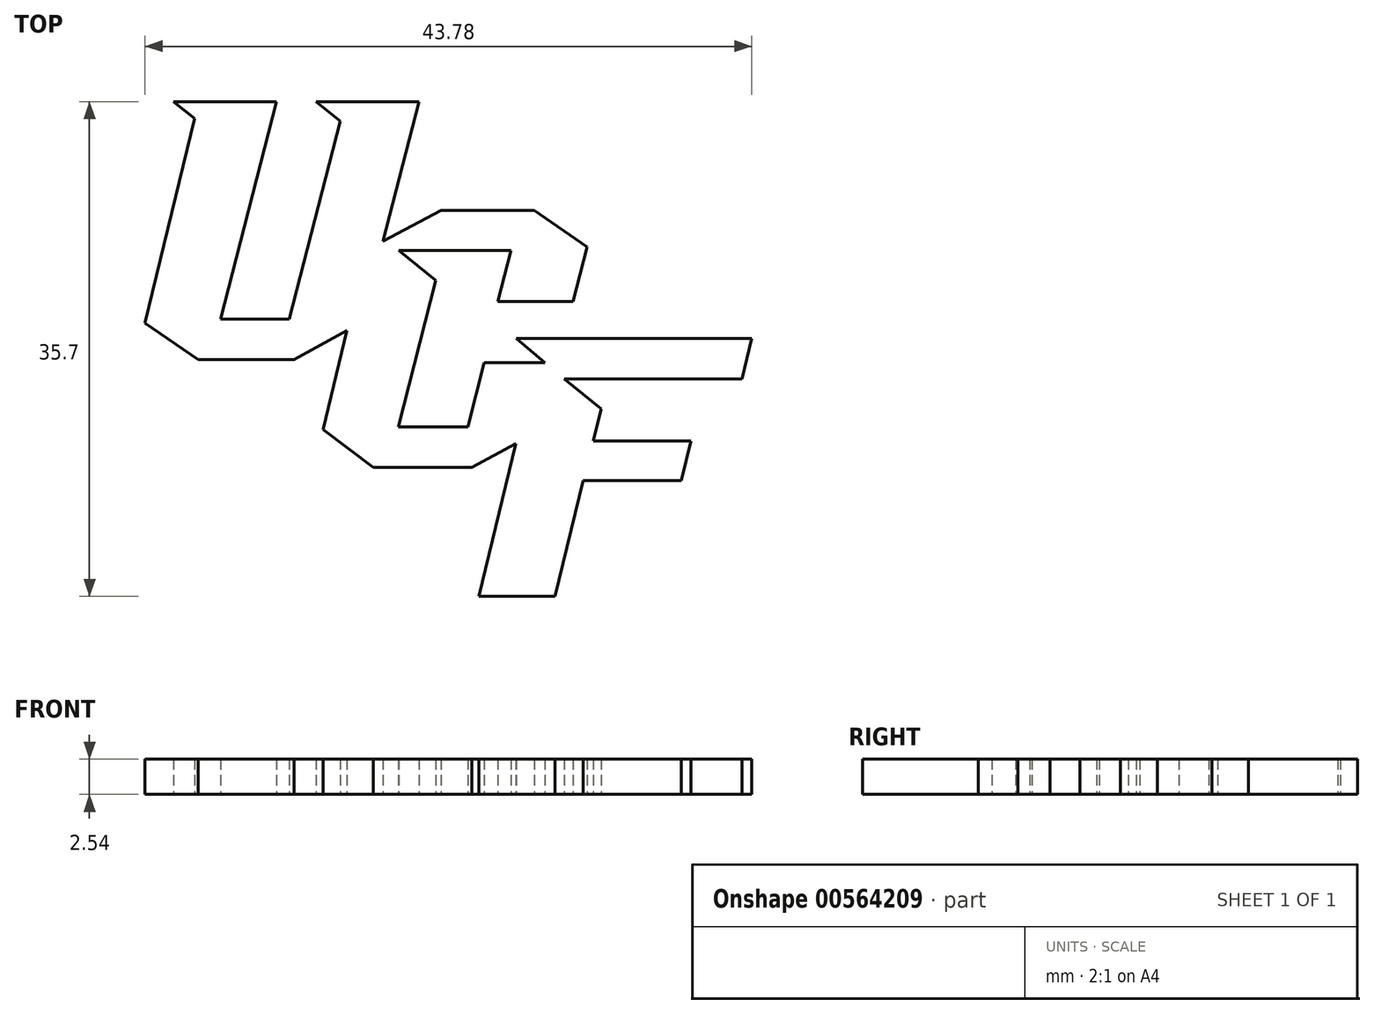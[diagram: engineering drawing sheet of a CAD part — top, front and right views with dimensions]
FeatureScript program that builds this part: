
annotation { "Feature Type Name" : "Feature", "Feature Type Description" : "" }
export const myFeature = defineFeature(function(context is Context, id is Id, definition is map)
    precondition{}
    {
        {
            var Q0;
            Q0=qCreatedBy(makeId("Top.planeOp"),FACE);
            var sketch = newSketch(context, id + "F0", { "sketchPlane" : qUnion([Q0])});
            skLineSegment(sketch, "E0", {"start": v(-24.4, 19.25) * mm, "end": v(2.19, 19.25) * mm});
            skLineSegment(sketch, "E1", {"start": v(2.19, 19.25) * mm, "end": v(0.35, 11.38) * mm});
            skLineSegment(sketch, "E2", {"start": v(0.35, 11.38) * mm, "end": v(8.5, 11.38) * mm});
            skLineSegment(sketch, "E3", {"start": v(8.5, 11.38) * mm, "end": v(14.26, 7.42) * mm});
            skLineSegment(sketch, "E4", {"start": v(14.26, 7.42) * mm, "end": v(12.9, 2.1) * mm});
            skLineSegment(sketch, "E5", {"start": v(12.9, 2.1) * mm, "end": v(26.4, 2.1) * mm});
            skLineSegment(sketch, "E6", {"start": v(26.4, 2.1) * mm, "end": v(24.63, -5.27) * mm});
            skLineSegment(sketch, "E7", {"start": v(24.63, -5.27) * mm, "end": v(21.92, -5.27) * mm});
            skLineSegment(sketch, "E8", {"start": v(21.92, -5.27) * mm, "end": v(20, -12.77) * mm});
            skLineSegment(sketch, "E9", {"start": v(20, -12.77) * mm, "end": v(13.09, -12.77) * mm});
            skLineSegment(sketch, "E10", {"start": v(13.09, -12.77) * mm, "end": v(10.99, -20.97) * mm});
            skLineSegment(sketch, "E11", {"start": v(10.99, -20.97) * mm, "end": v(0.94, -20.97) * mm});
            skLineSegment(sketch, "E12", {"start": v(0.94, -20.97) * mm, "end": v(3.33, -11.66) * mm});
            skLineSegment(sketch, "E13", {"start": v(3.33, -11.66) * mm, "end": v(-4.63, -11.66) * mm});
            skLineSegment(sketch, "E14", {"start": v(-4.63, -11.66) * mm, "end": v(-9.96, -7.66) * mm});
            skLineSegment(sketch, "E15", {"start": v(-9.96, -7.66) * mm, "end": v(-8.96, -3.76) * mm});
            skLineSegment(sketch, "E16", {"start": v(-8.96, -3.76) * mm, "end": v(-17.19, -3.76) * mm});
            skLineSegment(sketch, "E17", {"start": v(-17.19, -3.76) * mm, "end": v(-22.66, 0.35) * mm});
            skLineSegment(sketch, "E18", {"start": v(-22.66, 0.35) * mm, "end": v(-18.94, 14.88) * mm});
            skLineSegment(sketch, "E19", {"start": v(-18.94, 14.88) * mm, "end": v(-24.4, 19.25) * mm});
            skLineSegment(sketch, "E20", {"start": v(-17.04, 15.64) * mm, "end": v(-19.12, 17.3) * mm});
            skLineSegment(sketch, "E21", {"start": v(-19.12, 17.3) * mm, "end": v(-10.38, 17.3) * mm});
            skLineSegment(sketch, "E22", {"start": v(-10.38, 17.3) * mm, "end": v(-14.4, 1.61) * mm});
            skLineSegment(sketch, "E23", {"start": v(-14.4, 1.61) * mm, "end": v(-10.1, 1.61) * mm});
            skLineSegment(sketch, "E24", {"start": v(-10.1, 1.61) * mm, "end": v(-6.55, 15.47) * mm});
            skLineSegment(sketch, "E25", {"start": v(-6.55, 15.47) * mm, "end": v(-8.85, 17.3) * mm});
            skLineSegment(sketch, "E26", {"start": v(-8.85, 17.3) * mm, "end": v(-0.1, 17.3) * mm});
            skLineSegment(sketch, "E27", {"start": v(-0.1, 17.3) * mm, "end": v(-2.61, 7.52) * mm});
            skLineSegment(sketch, "E28", {"start": v(-2.61, 7.52) * mm, "end": v(1.02, 9.45) * mm});
            skLineSegment(sketch, "E29", {"start": v(1.02, 9.45) * mm, "end": v(7.92, 9.45) * mm});
            skLineSegment(sketch, "E30", {"start": v(7.92, 9.45) * mm, "end": v(12, 6.64) * mm});
            skLineSegment(sketch, "E31", {"start": v(12, 6.64) * mm, "end": v(10.87, 2.24) * mm});
            skLineSegment(sketch, "E32", {"start": v(10.87, 2.24) * mm, "end": v(4.77, 2.24) * mm});
            skLineSegment(sketch, "E33", {"start": v(4.77, 2.24) * mm, "end": v(5.72, 5.94) * mm});
            skLineSegment(sketch, "E34", {"start": v(5.72, 5.94) * mm, "end": v(-1.06, 5.94) * mm});
            skLineSegment(sketch, "E35", {"start": v(-1.06, 5.94) * mm, "end": v(1.06, 4.22) * mm});
            skLineSegment(sketch, "E36", {"start": v(1.06, 4.22) * mm, "end": v(-1.6, -6.17) * mm});
            skLineSegment(sketch, "E37", {"start": v(-1.6, -6.17) * mm, "end": v(2.76, -6.17) * mm});
            skLineSegment(sketch, "E38", {"start": v(2.76, -6.17) * mm, "end": v(3.95, -1.52) * mm});
            skLineSegment(sketch, "E39", {"start": v(3.95, -1.52) * mm, "end": v(7.7, -1.52) * mm});
            skLineSegment(sketch, "E40", {"start": v(7.7, -1.52) * mm, "end": v(5.66, 0.2) * mm});
            skLineSegment(sketch, "E41", {"start": v(5.66, 0.2) * mm, "end": v(23.91, 0.2) * mm});
            skLineSegment(sketch, "E42", {"start": v(23.91, 0.2) * mm, "end": v(23.06, -3.34) * mm});
            skLineSegment(sketch, "E43", {"start": v(23.06, -3.34) * mm, "end": v(10.87, -3.34) * mm});
            skLineSegment(sketch, "E44", {"start": v(10.87, -3.34) * mm, "end": v(13, -5.07) * mm});
            skLineSegment(sketch, "E45", {"start": v(13, -5.07) * mm, "end": v(12.48, -7.18) * mm});
            skLineSegment(sketch, "E46", {"start": v(12.48, -7.18) * mm, "end": v(19.51, -7.18) * mm});
            skLineSegment(sketch, "E47", {"start": v(19.51, -7.18) * mm, "end": v(18.67, -10.68) * mm});
            skLineSegment(sketch, "E48", {"start": v(18.67, -10.68) * mm, "end": v(11.58, -10.68) * mm});
            skLineSegment(sketch, "E49", {"start": v(11.58, -10.68) * mm, "end": v(9.57, -19.03) * mm});
            skLineSegment(sketch, "E50", {"start": v(9.57, -19.03) * mm, "end": v(3.4, -19.03) * mm});
            skLineSegment(sketch, "E51", {"start": v(3.4, -19.03) * mm, "end": v(6, -8.3) * mm});
            skLineSegment(sketch, "E52", {"start": v(6, -8.3) * mm, "end": v(3.39, -9.72) * mm});
            skLineSegment(sketch, "E53", {"start": v(3.39, -9.72) * mm, "end": v(-3.9, -9.72) * mm});
            skLineSegment(sketch, "E54", {"start": v(-3.9, -9.72) * mm, "end": v(-7.78, -6.8) * mm});
            skLineSegment(sketch, "E55", {"start": v(-7.78, -6.8) * mm, "end": v(-6.18, -0.17) * mm});
            skLineSegment(sketch, "E56", {"start": v(-6.18, -0.17) * mm, "end": v(-9.43, -1.94) * mm});
            skLineSegment(sketch, "E57", {"start": v(-9.43, -1.94) * mm, "end": v(-16.52, -1.94) * mm});
            skLineSegment(sketch, "E58", {"start": v(-16.52, -1.94) * mm, "end": v(-20.63, 0.89) * mm});
            skLineSegment(sketch, "E59", {"start": v(-20.63, 0.89) * mm, "end": v(-17.04, 15.64) * mm});
            skLineSegment(sketch, "E60", {"start": v(-19.66, 1.34) * mm, "end": v(-16.1, 15.94) * mm});
            skLineSegment(sketch, "E61", {"start": v(-16.1, 15.94) * mm, "end": v(-16.73, 16.44) * mm});
            skLineSegment(sketch, "E62", {"start": v(-16.73, 16.44) * mm, "end": v(-11.47, 16.44) * mm});
            skLineSegment(sketch, "E63", {"start": v(-11.47, 16.44) * mm, "end": v(-11.68, 15.58) * mm});
            skLineSegment(sketch, "E64", {"start": v(-11.68, 15.58) * mm, "end": v(-15.27, 15.58) * mm});
            skLineSegment(sketch, "E65", {"start": v(-15.27, 15.58) * mm, "end": v(-18.9, 0.72) * mm});
            skLineSegment(sketch, "E66", {"start": v(-18.9, 0.72) * mm, "end": v(-19.66, 1.34) * mm});
            skLineSegment(sketch, "E67", {"start": v(-9.5, 0.81) * mm, "end": v(-5.64, 15.85) * mm});
            skLineSegment(sketch, "E68", {"start": v(-5.64, 15.85) * mm, "end": v(-6.5, 16.54) * mm});
            skLineSegment(sketch, "E69", {"start": v(-6.5, 16.54) * mm, "end": v(-1.13, 16.54) * mm});
            skLineSegment(sketch, "E70", {"start": v(-1.13, 16.54) * mm, "end": v(-1.38, 15.56) * mm});
            skLineSegment(sketch, "E71", {"start": v(-1.38, 15.56) * mm, "end": v(-4.91, 15.56) * mm});
            skLineSegment(sketch, "E72", {"start": v(-4.91, 15.56) * mm, "end": v(-8.93, -0.1) * mm});
            skLineSegment(sketch, "E73", {"start": v(-8.93, -0.1) * mm, "end": v(-14.72, -0.1) * mm});
            skLineSegment(sketch, "E74", {"start": v(-14.72, -0.1) * mm, "end": v(-14.48, 0.81) * mm});
            skLineSegment(sketch, "E75", {"start": v(-14.48, 0.81) * mm, "end": v(-9.5, 0.81) * mm});
            skLineSegment(sketch, "E76", {"start": v(-6.84, -6.48) * mm, "end": v(-3.84, 6) * mm});
            skLineSegment(sketch, "E77", {"start": v(-3.84, 6) * mm, "end": v(1.18, 8.67) * mm});
            skLineSegment(sketch, "E78", {"start": v(1.18, 8.67) * mm, "end": v(7.59, 8.67) * mm});
            skLineSegment(sketch, "E79", {"start": v(7.59, 8.67) * mm, "end": v(8.81, 7.82) * mm});
            skLineSegment(sketch, "E80", {"start": v(8.81, 7.82) * mm, "end": v(1.49, 7.82) * mm});
            skLineSegment(sketch, "E81", {"start": v(1.49, 7.82) * mm, "end": v(-1.45, 6.26) * mm});
            skLineSegment(sketch, "E82", {"start": v(-2.96, 5.46) * mm, "end": v(-6, -7.13) * mm});
            skLineSegment(sketch, "E83", {"start": v(-6, -7.13) * mm, "end": v(-6.84, -6.48) * mm});
            skLineSegment(sketch, "E84", {"start": v(6.58, 5.94) * mm, "end": v(7.49, 5.94) * mm});
            skLineSegment(sketch, "E85", {"start": v(7.49, 5.94) * mm, "end": v(6.78, 3) * mm});
            skLineSegment(sketch, "E86", {"start": v(6.78, 3) * mm, "end": v(5.83, 3) * mm});
            skLineSegment(sketch, "E87", {"start": v(5.83, 3) * mm, "end": v(6.58, 5.94) * mm});
            skLineSegment(sketch, "E88", {"start": v(-1.67, -7) * mm, "end": v(3.4, -7) * mm});
            skLineSegment(sketch, "E89", {"start": v(3.4, -7) * mm, "end": v(4.52, -2.33) * mm});
            skLineSegment(sketch, "E90", {"start": v(4.52, -2.33) * mm, "end": v(7.2, -2.33) * mm});
            skLineSegment(sketch, "E91", {"start": v(7.2, -2.33) * mm, "end": v(7, -3.2) * mm});
            skLineSegment(sketch, "E92", {"start": v(7, -3.2) * mm, "end": v(5.23, -3.2) * mm});
            skLineSegment(sketch, "E93", {"start": v(5.23, -3.2) * mm, "end": v(4.11, -7.87) * mm});
            skLineSegment(sketch, "E94", {"start": v(4.11, -7.87) * mm, "end": v(-1.9, -7.87) * mm});
            skLineSegment(sketch, "E95", {"start": v(-1.9, -7.87) * mm, "end": v(-1.67, -7) * mm});
            skLineSegment(sketch, "E96", {"start": v(8.62, -1.17) * mm, "end": v(7.93, -0.7) * mm});
            skLineSegment(sketch, "E97", {"start": v(7.93, -0.7) * mm, "end": v(22.9, -0.7) * mm});
            skLineSegment(sketch, "E98", {"start": v(22.9, -0.7) * mm, "end": v(22.7, -1.52) * mm});
            skLineSegment(sketch, "E99", {"start": v(22.7, -1.52) * mm, "end": v(9.5, -1.52) * mm});
            skLineSegment(sketch, "E100", {"start": v(9.5, -1.52) * mm, "end": v(5.46, -18.24) * mm});
            skLineSegment(sketch, "E101", {"start": v(5.46, -18.24) * mm, "end": v(4.43, -18.24) * mm});
            skLineSegment(sketch, "E102", {"start": v(4.43, -18.24) * mm, "end": v(8.45, -1.84) * mm});
            skLineSegment(sketch, "E103", {"start": v(12.3, -7.95) * mm, "end": v(18.44, -7.95) * mm});
            skLineSegment(sketch, "E104", {"start": v(18.44, -7.95) * mm, "end": v(18.22, -8.86) * mm});
            skLineSegment(sketch, "E105", {"start": v(18.22, -8.86) * mm, "end": v(12.06, -8.86) * mm});
            skLineSegment(sketch, "E106", {"start": v(12.06, -8.86) * mm, "end": v(12.3, -7.95) * mm});
            skLineSegment(sketch, "E107.0", {"start": v(-20.27, 1.02) * mm, "end": v(-16.68, 15.76) * mm});
            skLineSegment(sketch, "E108.0", {"start": v(-14.8, 1.3) * mm, "end": v(-9.85, 1.3) * mm});
            skLineSegment(sketch, "E109.0", {"start": v(-9.85, 1.3) * mm, "end": v(-6.2, 15.59) * mm});
            skLineSegment(sketch, "E110.0", {"start": v(-6.2, 15.59) * mm, "end": v(-7.94, 17) * mm});
            skLineSegment(sketch, "E111.0", {"start": v(-0.51, 17) * mm, "end": v(-3.1, 6.9) * mm});
            skLineSegment(sketch, "E112.0", {"start": v(-3.1, 6.9) * mm, "end": v(1.1, 9.13) * mm});
            skLineSegment(sketch, "E113.0", {"start": v(1.1, 9.13) * mm, "end": v(7.82, 9.13) * mm});
            skLineSegment(sketch, "E114.0", {"start": v(7.82, 9.13) * mm, "end": v(11.63, 6.5) * mm});
            skLineSegment(sketch, "E115.0", {"start": v(11.63, 6.5) * mm, "end": v(10.62, 2.56) * mm});
            skLineSegment(sketch, "E116.0", {"start": v(10.62, 2.56) * mm, "end": v(5.18, 2.56) * mm});
            skLineSegment(sketch, "E117.0", {"start": v(6.13, 6.26) * mm, "end": v(-1.95, 6.26) * mm});
            skLineSegment(sketch, "E118.0", {"start": v(-1.95, 6.26) * mm, "end": v(0.7, 4.1) * mm});
            skLineSegment(sketch, "E119.0", {"start": v(0.7, 4.1) * mm, "end": v(-2, -6.49) * mm});
            skLineSegment(sketch, "E120.0", {"start": v(-5.7, 0.46) * mm, "end": v(-9.52, -1.63) * mm});
            skLineSegment(sketch, "E121.0", {"start": v(-7.42, -6.66) * mm, "end": v(-5.7, 0.46) * mm});
            skLineSegment(sketch, "E122.0", {"start": v(-9.52, -1.63) * mm, "end": v(-16.43, -1.63) * mm});
            skLineSegment(sketch, "E123.0", {"start": v(-2, -6.49) * mm, "end": v(3, -6.49) * mm});
            skLineSegment(sketch, "E124.0", {"start": v(3, -6.49) * mm, "end": v(4.2, -1.84) * mm});
            skLineSegment(sketch, "E125.0", {"start": v(4.2, -1.84) * mm, "end": v(8.56, -1.84) * mm});
            skLineSegment(sketch, "E126.0", {"start": v(8.56, -1.84) * mm, "end": v(6.53, -0.12) * mm});
            skLineSegment(sketch, "E127.0", {"start": v(22.8, -3.02) * mm, "end": v(9.98, -3.02) * mm});
            skLineSegment(sketch, "E128.0", {"start": v(9.98, -3.02) * mm, "end": v(12.63, -5.2) * mm});
            skLineSegment(sketch, "E129.0", {"start": v(12.63, -5.2) * mm, "end": v(12.08, -7.5) * mm});
            skLineSegment(sketch, "E130.0", {"start": v(12.08, -7.5) * mm, "end": v(19.1, -7.5) * mm});
            skLineSegment(sketch, "E131.0", {"start": v(-3.79, -9.4) * mm, "end": v(-7.42, -6.66) * mm});
            skLineSegment(sketch, "E132.0", {"start": v(3.3, -9.4) * mm, "end": v(-3.79, -9.4) * mm});
            skLineSegment(sketch, "E133.0", {"start": v(6.47, -7.68) * mm, "end": v(3.3, -9.4) * mm});
            skLineSegment(sketch, "E134.0", {"start": v(3.81, -18.71) * mm, "end": v(6.47, -7.68) * mm});
            skLineSegment(sketch, "E135.0", {"start": v(-16.43, -1.63) * mm, "end": v(-20.27, 1.02) * mm});
            skLineSegment(sketch, "E136.0", {"start": v(9.32, -18.71) * mm, "end": v(3.81, -18.71) * mm});
            skLineSegment(sketch, "E137.0", {"start": v(11.33, -10.37) * mm, "end": v(9.32, -18.71) * mm});
            skLineSegment(sketch, "E138.0", {"start": v(18.42, -10.37) * mm, "end": v(11.33, -10.37) * mm});
            skLineSegment(sketch, "E139.trimOffspring", {"start": v(-18.21, 17) * mm, "end": v(-10.79, 17) * mm});
            skLineSegment(sketch, "E140", {"start": v(-16.68, 15.76) * mm, "end": v(-18.21, 17) * mm});
            skLineSegment(sketch, "E141.trimOffspring", {"start": v(-10.79, 17) * mm, "end": v(-14.8, 1.3) * mm});
            skLineSegment(sketch, "E142.trimOffspring", {"start": v(-7.94, 17) * mm, "end": v(-0.51, 17) * mm});
            skLineSegment(sketch, "E143.trimOffspring", {"start": v(19.1, -7.5) * mm, "end": v(18.42, -10.37) * mm});
            skLineSegment(sketch, "E144.trimOffspring", {"start": v(23.5, -0.12) * mm, "end": v(22.8, -3.02) * mm});
            skLineSegment(sketch, "E145.trimOffspring", {"start": v(6.53, -0.12) * mm, "end": v(23.5, -0.12) * mm});
            skLineSegment(sketch, "E146.trimOffspring", {"start": v(5.18, 2.56) * mm, "end": v(6.13, 6.26) * mm});
            skLineSegment(sketch, "E147.trimOffspring", {"start": v(8.47, -1.76) * mm, "end": v(8.62, -1.17) * mm});
            skLineSegment(sketch, "E148.trimOffspring", {"start": v(-1.75, 6.1) * mm, "end": v(-2.96, 5.46) * mm});
            skSolve(sketch);
        }
        {
            var Q0;
            Q0=makeQuery(id+"F0.imprint","IMPRINT",FACE,{"disambiguationData":[TD([[makeQuery(id+"F0.imprint","IMPRINT",EDGE,{"derivedFrom":sQuery(id+"F0.wireOp",EDGE,"E60")}),1.0]])]});
            var Q1;
            Q1=makeQuery(id+"F0.imprint","IMPRINT",FACE,{"disambiguationData":[TD([[makeQuery(id+"F0.imprint","IMPRINT",EDGE,{"derivedFrom":sQuery(id+"F0.wireOp",EDGE,"E76")}),-1.0]])]});
            var Q2;
            Q2=makeQuery(id+"F0.imprint","IMPRINT",FACE,{"disambiguationData":[TD([[makeQuery(id+"F0.imprint","IMPRINT",EDGE,{"derivedFrom":sQuery(id+"F0.wireOp",EDGE,"E67")}),-1.0]])]});
            var Q3;
            Q3=makeQuery(id+"F0.imprint","IMPRINT",FACE,{"disambiguationData":[TD([[makeQuery(id+"F0.imprint","IMPRINT",EDGE,{"derivedFrom":sQuery(id+"F0.wireOp",EDGE,"E60")}),-1.0]])]});
            var Q4;
            Q4=makeQuery(id+"F0.imprint","IMPRINT",FACE,{"disambiguationData":[TD([[makeQuery(id+"F0.imprint","IMPRINT",EDGE,{"derivedFrom":sQuery(id+"F0.wireOp",EDGE,"E84")}),-1.0]])]});
            var Q5;
            Q5=makeQuery(id+"F0.imprint","IMPRINT",FACE,{"disambiguationData":[TD([[makeQuery(id+"F0.imprint","IMPRINT",EDGE,{"derivedFrom":sQuery(id+"F0.wireOp",EDGE,"E96")}),-1.0]])]});
            var Q6;
            Q6=makeQuery(id+"F0.imprint","IMPRINT",FACE,{"disambiguationData":[TD([[makeQuery(id+"F0.imprint","IMPRINT",EDGE,{"derivedFrom":sQuery(id+"F0.wireOp",EDGE,"E88")}),-1.0]])]});
            var Q7;
            Q7=makeQuery(id+"F0.imprint","IMPRINT",FACE,{"disambiguationData":[TD([[makeQuery(id+"F0.imprint","IMPRINT",EDGE,{"derivedFrom":sQuery(id+"F0.wireOp",EDGE,"E103")}),-1.0]])]});
            extrude(context, id + "F1", {"entities" : qUnion([Q0, Q1, Q2, Q3, Q4, Q5, Q6, Q7]), "depth" : 2.54 * mm, "offsetDistance" : 25.4 * mm});
        }
    });
